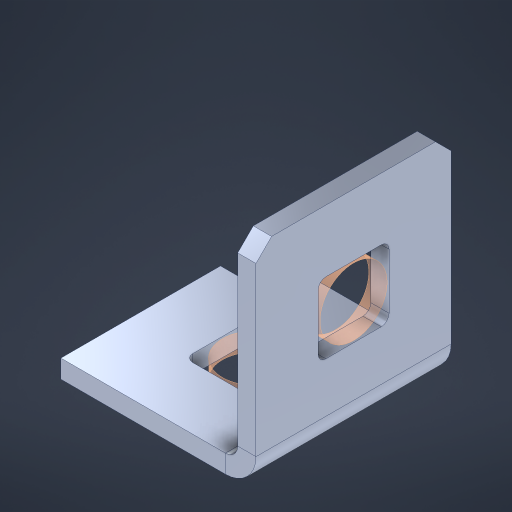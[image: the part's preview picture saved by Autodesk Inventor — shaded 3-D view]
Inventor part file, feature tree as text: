
AUTODESK INVENTOR PART (.ipt)
format: ipt  version: 2023 (Build 270158000, 158)  size: 473,088 bytes
history: native  units: in
note: dims shown in document units (in); Inventor stores cm internally (conversion verified against a paired STEP export)
features: other x12, sheet_metal_op x11, sketch x10, extrude x3, pattern_linear x2, mirror x1, chamfer x1
ambient origin geometry x8: Origin, YZ Plane, XZ Plane, XY Plane, X Axis, Y Axis, Z Axis, Center Point
bodies: Solid1 (feature_tree), Body (feature_tree)
feature tree (40):
  sheet_metal_op  "Flanges"
  other  "Flange Pattern Plane"
  other  "Flange Pattern Sketch"
  sheet_metal_op  "Flange Pattern"
  sheet_metal_op  "Body Pattern"
  pattern_linear  "Center Pattern"  Spacing1=0.0469in  [1 undecoded]
  other  "Arc Length"
  mirror  "Notch Mirror"
  pattern_linear  "Notch Pattern"  Spacing1=0.182in  [1 undecoded]
  chamfer  "End Chamfer"
  extrude  "Half Cut"  Depth=0.02in
  sketch  "Sketch1"  dims[d0=1.0in]
  other  "Plate1"
  sketch  "Sketch2"  dims[d1=0.5in]
  other  "Plate2"
  sheet_metal_op  "Bend1"
  sheet_metal_op  "Corner1"
  sketch  "Sketch3"  dims[d2=0.0469in]
  sketch  "Sketch7"  dims[d3=0.0469in]
  other  "Srf1"
  other  "Srf2"
  sketch  "Sketch8"  dims[d4=0.0234in]
  sketch  "Sketch9"  dims[d5=0.0938in]
  other  "Srf91"
  sheet_metal_op  "Body Pattern Sketch"
  other  "Srf92"
  sketch  "Sketch13"  dims[d6=0.0469in]
  sketch  "Sketch14"  dims[d7=0.5in d8=90.0deg d9=0.0312in]
  sketch  "Sketch15"  dims[d10=0.1875in]
  sketch  "Sketch16"  dims[d11=0.0469in d12=0.0469in d16=0.182in d17=0.02in d18=0.0469in d19=0.0in d20=0.25in d21=0.25in d38=0.3937in d40=0.5in d41=0.3937in d43=1.0in d46=0.172in d47=1.0in d48=0.0in d49=0.182in d50=0.02in d51=0.25in d52=0.25in d53=0.0469in d54=0.0in d55=0.172in d56=1.0in d57=0.0in d58=0.25in d60=0.3937in d62=0.5in d63=0.3937in d65=0.5in d85=0.1227in d86=0.1659in d88=0.04in d89=0.0469in d90=0.0in d91=0.04in d92=0.0491in d95=2.5in d96=0.04in d97=0.25in d98=45.0deg d99=0.25in d100=0.5in d101=0.0in d102=2.497in d106=0.182in d107=0.02in d108=0.5in d109=0.5in d110=0.0469in d111=0.0in d112=0.172in d113=0.5in d114=0.0in d117=0.5in d118=0.5in d119=0.5in]
  other  "Srf786"
  sheet_metal_op  "Flange Stamp"
  sheet_metal_op  "Flange Circle"
  sheet_metal_op  "Body Stamp"
  sheet_metal_op  "Body Circle"
  other  "Center Stamp"
  other  "Center Circle"
  sheet_metal_op  "Notch"
  extrude  "ExtrusionSrf2"  Depth=0.0469in
  extrude  "ExtrusionSrf92"  TaperAngle=0.0deg  [1 undecoded]
note: 3 required parameter values undecoded (feature->parameter linkage not recoverable at this tier; creation-order binding heuristic only, values carry confidence <= 0.55)
